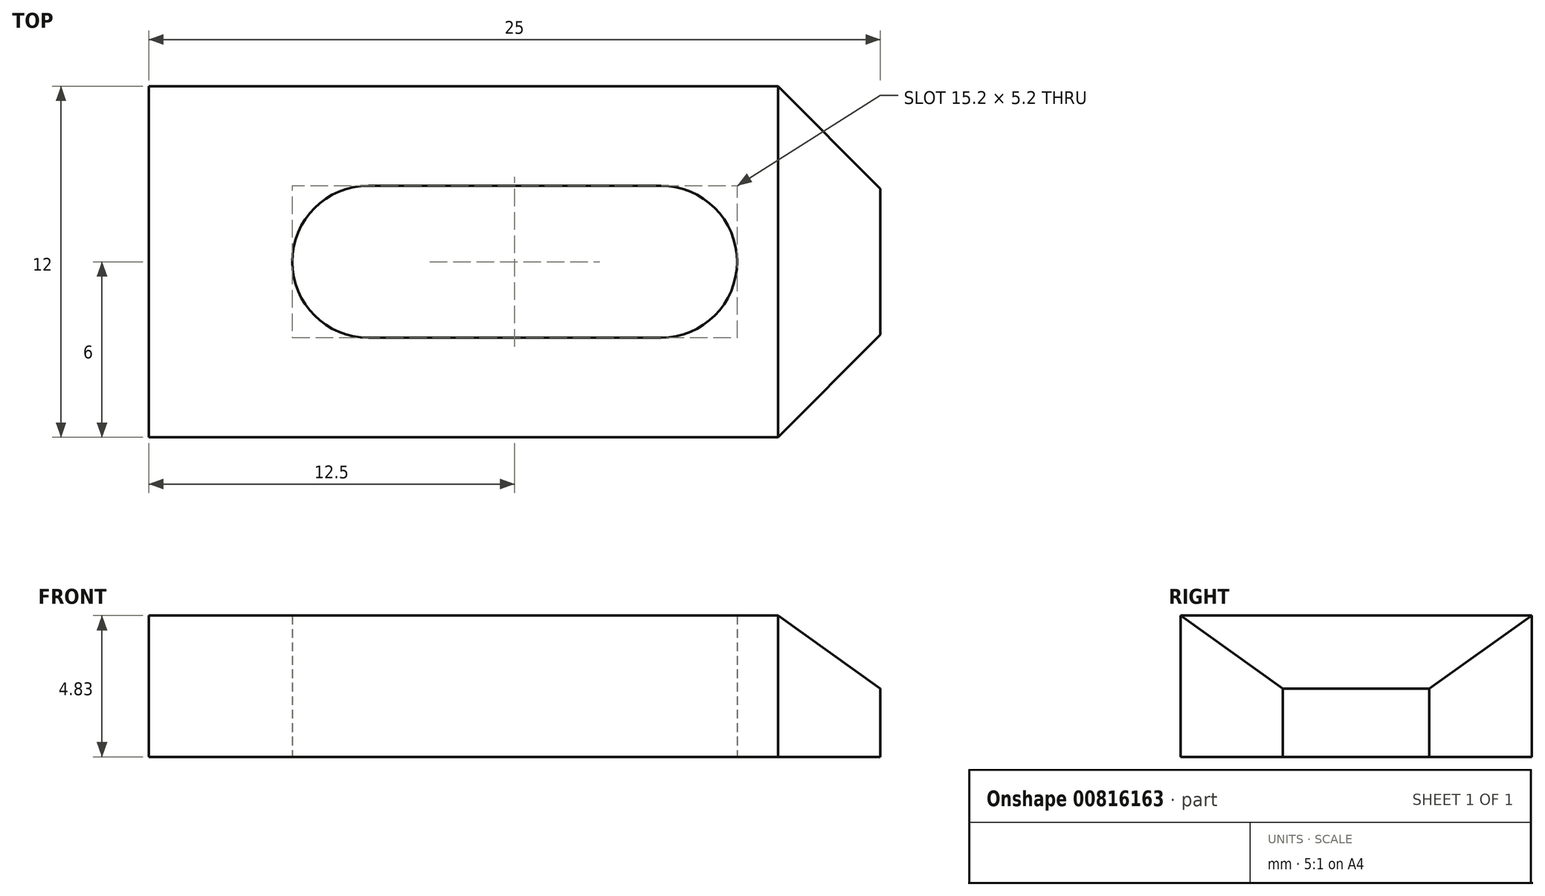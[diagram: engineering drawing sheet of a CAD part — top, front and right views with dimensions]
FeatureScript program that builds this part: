
annotation { "Feature Type Name" : "Feature", "Feature Type Description" : "" }
export const myFeature = defineFeature(function(context is Context, id is Id, definition is map)
    precondition{}
    {
        {
            var Q0;
            Q0=qCreatedBy(makeId("Top.planeOp"),FACE);
            var sketch = newSketch(context, id + "F0", { "sketchPlane" : qUnion([Q0])});
            skLineSegment(sketch, "E0", {"start": v(-5, 0) * mm, "end": v(5, 0) * mm});
            skLineSegment(sketch, "E1.bottom", {"start": v(9, -6) * mm, "end": v(-12.5, -6) * mm});
            skLineSegment(sketch, "E1.top", {"start": v(9, 6) * mm, "end": v(-12.5, 6) * mm});
            skLineSegment(sketch, "E1.left", {"start": v(12.5, -2.5) * mm, "end": v(12.5, 2.5) * mm});
            skLineSegment(sketch, "E1.right", {"start": v(-12.5, -6) * mm, "end": v(-12.5, 6) * mm});
            skPoint(sketch, "E1.middle", {"position": v(0, 0) * mm});
            skArc(sketch, "E2.0.startCap", {"start": v(-5, -2.6) * mm, "mid": v(-7.6, 0) * mm, "end": v(-5, 2.6) * mm});
            skArc(sketch, "E2.0.endCap", {"start": v(5, 2.6) * mm, "mid": v(7.6, 0) * mm, "end": v(5, -2.6) * mm});
            skLineSegment(sketch, "E2.0.left", {"start": v(-5, 2.6) * mm, "end": v(5, 2.6) * mm});
            skLineSegment(sketch, "E2.0.right", {"start": v(-5, -2.6) * mm, "end": v(5, -2.6) * mm});
            skLineSegment(sketch, "E3", {"start": v(9, 6) * mm, "end": v(12.5, 2.5) * mm});
            skLineSegment(sketch, "E4", {"start": v(12.5, -2.5) * mm, "end": v(9, -6) * mm});
            skPoint(sketch, "E5.orphan", {"position": v(12.5, 6) * mm});
            skPoint(sketch, "E6.orphan", {"position": v(12.5, -6) * mm});
            skPoint(sketch, "E7.visualSharp", {"position": v(-12.5, 6) * mm});
            skPoint(sketch, "E8.visualSharp", {"position": v(-12.5, -6) * mm});
            skSolve(sketch);
        }
        {
            var Q0;
            Q0=makeQuery(id+"F0.imprint","IMPRINT",FACE,{"disambiguationData":[TD([[makeQuery(id+"F0.imprint","IMPRINT",EDGE,{"derivedFrom":sQuery(id+"F0.wireOp",EDGE,"E1.bottom")}),-1.0]])]});
            extrude(context, id + "F1", {"entities" : qUnion([Q0]), "depth" : 4.83 * mm, "offsetDistance" : 25 * mm});
        }
        {
            var Q0;
            Q0=makeQuery(id+"F1.opExtrude","CAP_EDGE",EDGE,{"disambiguationData":[OSD([sQuery(id+"F0.wireOp",EDGE,"E1.left")])],"isStart":false});
            chamfer(context, id + "F2", {"entities" : qUnion([Q0]), "chamferType" : ChamferType.TWO_OFFSETS, "width1" : 3.5 * mm, "oppositeDirection" : false, "width2" : 2.5 * mm, "tangentPropagation" : true});
        }
    });
